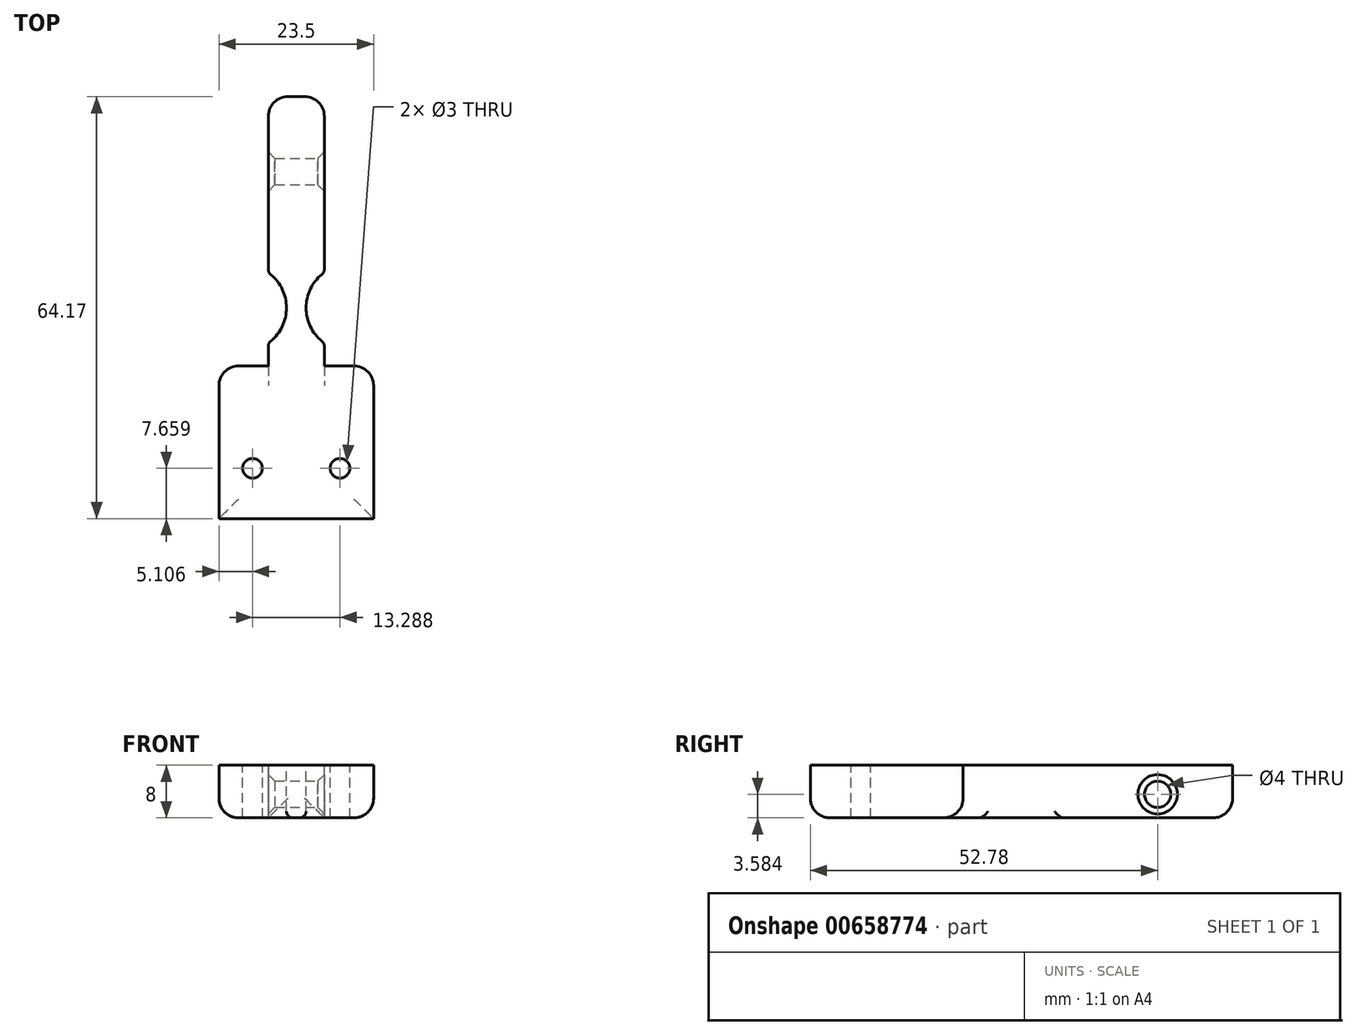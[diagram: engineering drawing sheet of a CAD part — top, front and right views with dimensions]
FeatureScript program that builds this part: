
annotation { "Feature Type Name" : "Feature", "Feature Type Description" : "" }
export const myFeature = defineFeature(function(context is Context, id is Id, definition is map)
    precondition{}
    {
        {
            var Q0;
            Q0=qCreatedBy(makeId("Top.planeOp"),FACE);
            var sketch = newSketch(context, id + "F0", { "sketchPlane" : qUnion([Q0])});
            skLineSegment(sketch, "E0.bottom", {"start": v(11.75, 59.42) * mm, "end": v(-11.75, 59.42) * mm});
            skLineSegment(sketch, "E0.top", {"start": v(11.75, 36.2) * mm, "end": v(-11.75, 36.2) * mm});
            skLineSegment(sketch, "E0.left", {"start": v(11.75, 59.42) * mm, "end": v(11.75, 36.2) * mm});
            skLineSegment(sketch, "E0.right", {"start": v(-11.75, 59.42) * mm, "end": v(-11.75, 36.2) * mm});
            skPoint(sketch, "E0.middle", {"position": v(0, 47.8) * mm});
            skLineSegment(sketch, "E1.bottom", {"start": v(4.26, 100.37) * mm, "end": v(-4.25, 100.37) * mm});
            skLineSegment(sketch, "E1.top", {"start": v(4.26, 40.65) * mm, "end": v(-4.25, 40.65) * mm});
            skLineSegment(sketch, "E1.left", {"start": v(4.26, 100.37) * mm, "end": v(4.26, 40.65) * mm});
            skLineSegment(sketch, "E1.right", {"start": v(-4.25, 100.37) * mm, "end": v(-4.25, 40.65) * mm});
            skSolve(sketch);
        }
        {
            var Q0;
            Q0=qSketchRegion(id+"F0",true);
            extrude(context, id + "F1", {"entities" : qUnion([Q0]), "oppositeDirection" : true, "depth" : 8 * mm, "offsetDistance" : 25 * mm});
        }
        {
            var Q0;
            Q0=makeQuery(id+"F1.opExtrude","SWEPT_EDGE",EDGE,{"disambiguationData":[OSD([sQuery(id+"F0.wireOp",EDGE,"E0.bottom"),sQuery(id+"F0.wireOp",EDGE,"E0.right")])]});
            var Q1;
            Q1=makeQuery(id+"F1.opExtrude","SWEPT_EDGE",EDGE,{"disambiguationData":[OSD([sQuery(id+"F0.wireOp",EDGE,"E0.bottom"),sQuery(id+"F0.wireOp",EDGE,"E0.left")])]});
            var Q2;
            Q2=makeQuery(id+"F1.opExtrude","SWEPT_EDGE",EDGE,{"disambiguationData":[OSD([sQuery(id+"F0.wireOp",EDGE,"E1.bottom"),sQuery(id+"F0.wireOp",EDGE,"E1.right")])]});
            var Q3;
            Q3=makeQuery(id+"F1.opExtrude","SWEPT_EDGE",EDGE,{"disambiguationData":[OSD([sQuery(id+"F0.wireOp",EDGE,"E1.bottom"),sQuery(id+"F0.wireOp",EDGE,"E1.left")])]});
            var Q4;
            Q4=makeQuery(id+"F1.opExtrude","CAP_EDGE",EDGE,{"disambiguationData":[OSD([sQuery(id+"F0.wireOp",EDGE,"E0.top")])],"isStart":false});
            var Q5;
            {var subQ0=sQuery(id+"F0.wireOp",EDGE,"E0.bottom");Q5=makeQuery(id+"F1.opExtrude","CAP_EDGE",EDGE,{"disambiguationData":[OSD([subQ0]),TDD([makeQuery(id+"F0.imprint","IMPRINT",EDGE,{"disambiguationData":[TD([[makeQuery(id+"F0.imprint","INTERSECT",VERTEX,{"derivedFrom":[subQ0,sQuery(id+"F0.wireOp",EDGE,"E0.right")]}),1.0]])],"derivedFrom":subQ0})])],"isStart":false});}
            var Q6;
            {var subQ0=sQuery(id+"F0.wireOp",EDGE,"E0.bottom");Q6=makeQuery(id+"F1.opExtrude","CAP_EDGE",EDGE,{"disambiguationData":[OSD([subQ0]),TDD([makeQuery(id+"F0.imprint","IMPRINT",EDGE,{"disambiguationData":[TD([[makeQuery(id+"F0.imprint","INTERSECT",VERTEX,{"derivedFrom":[subQ0,sQuery(id+"F0.wireOp",EDGE,"E0.left")]}),-1.0]])],"derivedFrom":subQ0})])],"isStart":false});}
            var Q7;
            Q7=makeQuery(id+"F1.opExtrude","CAP_EDGE",EDGE,{"disambiguationData":[OSD([sQuery(id+"F0.wireOp",EDGE,"E0.right")])],"isStart":false});
            var Q8;
            Q8=makeQuery(id+"F1.opExtrude","CAP_EDGE",EDGE,{"disambiguationData":[OSD([sQuery(id+"F0.wireOp",EDGE,"E0.left")])],"isStart":false});
            var Q9;
            Q9=makeQuery(id+"F1.opExtrude","CAP_EDGE",EDGE,{"disambiguationData":[OSD([sQuery(id+"F0.wireOp",EDGE,"E1.bottom")])],"isStart":false});
            fillet(context, id + "F2", {"entities" : qUnion([Q0, Q1, Q2, Q3, Q4, Q5, Q6, Q7, Q8, Q9]), "radius" : 3 * mm, "tangentPropagation" : true, "allowEdgeOverflow" : false});
        }
        {
            var Q0;
            Q0=qCreatedBy(makeId("Top.planeOp"),FACE);
            var sketch = newSketch(context, id + "F3", { "sketchPlane" : qUnion([Q0])});
            skCircle(sketch, "E2", {"center": v(-6.64, 43.86) * mm, "radius": 1.5 * mm});
            skCircle(sketch, "E3.MirrorC", {"center": v(6.64, 43.86) * mm, "radius": 1.5 * mm});
            skSolve(sketch);
        }
        {
            var Q0;
            Q0=qSketchRegion(id+"F3",true);
            extrude(context, id + "F4", {"entities" : qUnion([Q0]), "operationType" : NewBodyOperationType.REMOVE, "oppositeDirection" : true, "depth" : 25 * mm, "offsetDistance" : 25 * mm});
        }
        {
            var Q0;
            Q0=qCreatedBy(makeId("Right.planeOp"),FACE);
            var sketch = newSketch(context, id + "F5", { "sketchPlane" : qUnion([Q0])});
            skCircle(sketch, "E4", {"center": v(88.98, -4.42) * mm, "radius": 2 * mm});
            skSolve(sketch);
        }
        {
            var Q0;
            Q0=qSketchRegion(id+"F5",true);
            extrude(context, id + "F6", {"entities" : qUnion([Q0]), "operationType" : NewBodyOperationType.REMOVE, "oppositeDirection" : true, "depth" : 13.4 * mm, "offsetDistance" : 25 * mm, "hasSecondDirection" : true, "secondDirectionOppositeDirection" : false, "secondDirectionDepth" : 25 * mm});
        }
        {
            var Q0;
            Q0=makeQuery(id+"F6.boolean.opBoolean","INTERSECT",EDGE,{"derivedFrom":[makeQuery(id+"F1.opExtrude","SWEPT_FACE",FACE,{"disambiguationData":[OSD([sQuery(id+"F0.wireOp",EDGE,"E1.left")])]}),makeQuery(id+"F6.opExtrude","SWEPT_FACE",FACE,{"disambiguationData":[OSD([sQuery(id+"F5.wireOp",EDGE,"E4")])]})]});
            var Q1;
            Q1=makeQuery(id+"F6.boolean.opBoolean","INTERSECT",EDGE,{"derivedFrom":[makeQuery(id+"F1.opExtrude","SWEPT_FACE",FACE,{"disambiguationData":[OSD([sQuery(id+"F0.wireOp",EDGE,"E1.right")])]}),makeQuery(id+"F6.opExtrude","SWEPT_FACE",FACE,{"disambiguationData":[OSD([sQuery(id+"F5.wireOp",EDGE,"E4")])]})]});
            chamfer(context, id + "F7", {"entities" : qUnion([Q0, Q1]), "width" : 1 * mm, "tangentPropagation" : true});
        }
        {
            var Q0;
            Q0=qCreatedBy(makeId("Top.planeOp"),FACE);
            var sketch = newSketch(context, id + "F8", { "sketchPlane" : qUnion([Q0])});
            skCircle(sketch, "E5", {"center": v(8.07, 68.27) * mm, "radius": 6.58 * mm});
            skCircle(sketch, "E6.MirrorC", {"center": v(-8.07, 68.27) * mm, "radius": 6.58 * mm});
            skSolve(sketch);
        }
        {
            var Q0;
            Q0=qSketchRegion(id+"F8",true);
            extrude(context, id + "F9", {"entities" : qUnion([Q0]), "operationType" : NewBodyOperationType.REMOVE, "oppositeDirection" : true, "depth" : 25 * mm, "offsetDistance" : 25 * mm});
        }
        {
            var Q0;
            Q0=makeQuery(id+"F9.boolean.opBoolean","INTERSECT",EDGE,{"derivedFrom":[makeQuery(id+"F1.opExtrude","CAP_FACE",FACE,{"disambiguationData":[OSD([sQuery(id+"F0.wireOp",EDGE,"E0.bottom"),sQuery(id+"F0.wireOp",EDGE,"E0.top"),sQuery(id+"F0.wireOp",EDGE,"E0.left"),sQuery(id+"F0.wireOp",EDGE,"E0.right"),sQuery(id+"F0.wireOp",EDGE,"E1.bottom"),sQuery(id+"F0.wireOp",EDGE,"E1.left"),sQuery(id+"F0.wireOp",EDGE,"E1.right")])],"isStart":false}),makeQuery(id+"F9.opExtrude","SWEPT_FACE",FACE,{"disambiguationData":[OSD([sQuery(id+"F8.wireOp",EDGE,"E6.MirrorC")])]})]});
            var Q1;
            Q1=makeQuery(id+"F9.boolean.opBoolean","INTERSECT",EDGE,{"derivedFrom":[makeQuery(id+"F1.opExtrude","CAP_FACE",FACE,{"disambiguationData":[OSD([sQuery(id+"F0.wireOp",EDGE,"E0.bottom"),sQuery(id+"F0.wireOp",EDGE,"E0.top"),sQuery(id+"F0.wireOp",EDGE,"E0.left"),sQuery(id+"F0.wireOp",EDGE,"E0.right"),sQuery(id+"F0.wireOp",EDGE,"E1.bottom"),sQuery(id+"F0.wireOp",EDGE,"E1.left"),sQuery(id+"F0.wireOp",EDGE,"E1.right")])],"isStart":false}),makeQuery(id+"F9.opExtrude","SWEPT_FACE",FACE,{"disambiguationData":[OSD([sQuery(id+"F8.wireOp",EDGE,"E5")])]})]});
            var Q2;
            Q2=makeQuery(id+"F9.boolean.opBoolean","INTERSECT",EDGE,{"disambiguationData":[OD(1.0)],"derivedFrom":[makeQuery(id+"F1.opExtrude","SWEPT_FACE",FACE,{"disambiguationData":[OSD([sQuery(id+"F0.wireOp",EDGE,"E1.left")])]}),makeQuery(id+"F9.opExtrude","SWEPT_FACE",FACE,{"disambiguationData":[OSD([sQuery(id+"F8.wireOp",EDGE,"E5")])]})]});
            var Q3;
            Q3=makeQuery(id+"F9.boolean.opBoolean","INTERSECT",EDGE,{"disambiguationData":[OD(0.0)],"derivedFrom":[makeQuery(id+"F1.opExtrude","SWEPT_FACE",FACE,{"disambiguationData":[OSD([sQuery(id+"F0.wireOp",EDGE,"E1.left")])]}),makeQuery(id+"F9.opExtrude","SWEPT_FACE",FACE,{"disambiguationData":[OSD([sQuery(id+"F8.wireOp",EDGE,"E5")])]})]});
            var Q4;
            Q4=makeQuery(id+"F9.boolean.opBoolean","INTERSECT",EDGE,{"disambiguationData":[OD(1.0)],"derivedFrom":[makeQuery(id+"F1.opExtrude","SWEPT_FACE",FACE,{"disambiguationData":[OSD([sQuery(id+"F0.wireOp",EDGE,"E1.right")])]}),makeQuery(id+"F9.opExtrude","SWEPT_FACE",FACE,{"disambiguationData":[OSD([sQuery(id+"F8.wireOp",EDGE,"E6.MirrorC")])]})]});
            var Q5;
            Q5=makeQuery(id+"F9.boolean.opBoolean","INTERSECT",EDGE,{"disambiguationData":[OD(0.0)],"derivedFrom":[makeQuery(id+"F1.opExtrude","SWEPT_FACE",FACE,{"disambiguationData":[OSD([sQuery(id+"F0.wireOp",EDGE,"E1.right")])]}),makeQuery(id+"F9.opExtrude","SWEPT_FACE",FACE,{"disambiguationData":[OSD([sQuery(id+"F8.wireOp",EDGE,"E6.MirrorC")])]})]});
            fillet(context, id + "F10", {"entities" : qUnion([Q0, Q1, Q2, Q3, Q4, Q5]), "radius" : 1 * mm, "tangentPropagation" : true, "allowEdgeOverflow" : false});
        }
    });
